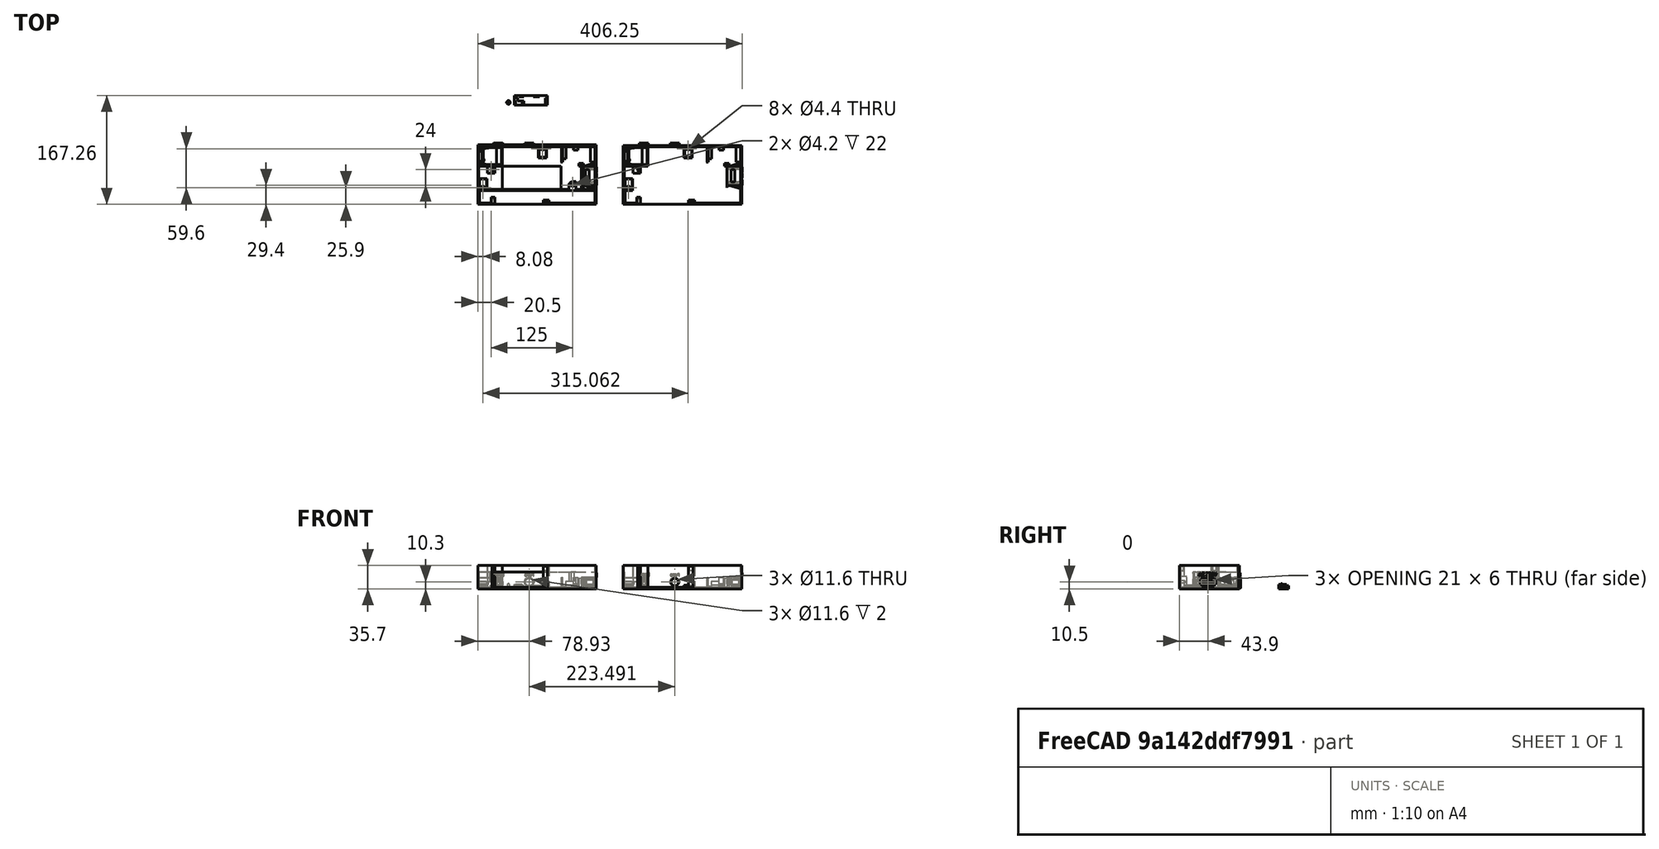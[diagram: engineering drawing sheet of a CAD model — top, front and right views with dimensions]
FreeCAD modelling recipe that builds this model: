
FCSTD DOCUMENT  (FreeCAD 0.19R)
Label: station.pump.1x12V
License: All rights reserved
LicenseURL: http://en.wikipedia.org/wiki/All_rights_reserved
objects: Part::Extrusion×91, Part::Feature×66, Part::MultiFuse×48, Part::Part2DObjectPython×42, Part::Cut×35, Part::FeaturePython×18, Part::Refine×12, Part::Cone×2, App::DocumentObjectGroup×2
note: 314 computed .brp shape members not serialized (recipe doc carries the construction recipe); baked Part::Feature solids carry a one-line shape summary decoded from their .brp

FEATURE [Part::Cut] Cut008
FEATURE [Part::Feature] Cut008_solid  label="Cut008 (Solid)"
  shape: bbox 182.8 x 74.77 x 26 mm, 631 faces (baked)
FEATURE [Part::Feature] Fusion005002002014004003003002009002010004002003006003008008004007002004008002005001  label="Fusion005002002014004003003002009002010004002003006003008008004007002004008002006"
  Placement = pos=(-44.5951,70.6176,187.501) rot=(0,0,1;1.5708rad)
  shape: bbox 50.9 x 14.8 x 7 mm, 30 faces (baked)
FEATURE [Part::MultiFuse] Fusion005002002014004003003002009002010004002003006003008008004007002004008002003
  Placement = pos=(333.004,49.2743,2.13395) rot=(0,0,1;0rad)
FEATURE [Part::Part2DObjectPython] Rectangle  # Draft 2D object (typed FeaturePython)
  Area = 4964
  ChamferSize = 0
  Columns = 1
  FilletRadius = 0
  Height = 136
  Length = 36.5
  MakeFace = true
  Placement = pos=(136,3,22) rot=(0,0,1;1.5708rad)
  Rows = 1
FEATURE [Part::Extrusion] Extrusion
  Base = -> Rectangle
  Dir = (-8.1519e-11,-1.28811e-08,-2)
  DirMode = 0
  FaceMakerClass = Part::FaceMakerBullseye
  LengthFwd = 0
  LengthRev = 0
  Solid = true
  Symmetric = false
FEATURE [Part::Cut] Cut
  Base = -> Cut008_solid
  Tool = -> Extrusion
FEATURE [Part::Part2DObjectPython] Rectangle001  # Draft 2D object (typed FeaturePython)
  Area = 5003.74
  ChamferSize = 0
  Columns = 1
  FilletRadius = 0
  Height = 49.6839
  Length = 100.711
  MakeFace = true
  Placement = pos=(166.761,-20.8491,-24.6542) rot=(0.57735,0.57735,0.57735;2.0944rad)
  Rows = 1
FEATURE [Part::FeaturePython] Slice  # WARN: FeaturePython — macro-defined, semantics opaque (R4)
  Base = -> Cut
  Mode = 1
  Tolerance = 0
  Tools = -> [Rectangle001]
FEATURE [Part::FeaturePython] Slice_child0  label="Slice.0"  # WARN: FeaturePython — macro-defined, semantics opaque (R4)
  Base = -> Slice
  FilterType = 1
  Invert = false
  OverrideMaxVal = 0
  WindowFrom = 80
  WindowTo = 100
  items = 0
FEATURE [Part::FeaturePython] Slice_child1  label="Slice.1"  # WARN: FeaturePython — macro-defined, semantics opaque (R4)
  Base = -> Slice
  FilterType = 1
  Invert = false
  OverrideMaxVal = 0
  WindowFrom = 80
  WindowTo = 100
  items = 1
FEATURE [Part::FeaturePython] Slice_child2  label="Slice.2"  # WARN: FeaturePython — macro-defined, semantics opaque (R4)
  Base = -> Slice
  FilterType = 1
  Invert = false
  OverrideMaxVal = 0
  WindowFrom = 80
  WindowTo = 100
  items = 2
FEATURE [Part::FeaturePython] Slice_child3  label="Slice.3"  # WARN: FeaturePython — macro-defined, semantics opaque (R4)
  Base = -> Slice
  FilterType = 1
  Invert = false
  OverrideMaxVal = 0
  WindowFrom = 80
  WindowTo = 100
  items = 3
FEATURE [Part::FeaturePython] Slice_child4  label="Slice.4"  # WARN: FeaturePython — macro-defined, semantics opaque (R4)
  Base = -> Slice
  FilterType = 1
  Invert = false
  OverrideMaxVal = 0
  WindowFrom = 80
  WindowTo = 100
  items = 4
FEATURE [Part::FeaturePython] Slice_child5  label="Slice.5"  # WARN: FeaturePython — macro-defined, semantics opaque (R4)
  Base = -> Slice
  FilterType = 1
  Invert = false
  OverrideMaxVal = 0
  WindowFrom = 80
  WindowTo = 100
  items = 5
FEATURE [Part::FeaturePython] Slice_child6  label="Slice.6"  # WARN: FeaturePython — macro-defined, semantics opaque (R4)
  Base = -> Slice
  FilterType = 1
  Invert = false
  OverrideMaxVal = 0
  WindowFrom = 80
  WindowTo = 100
  items = 6
FEATURE [Part::MultiFuse] Fusion
  Placement = pos=(4.18709e-10,0,2) rot=(0,0,1;0rad)
  Shapes = -> [Slice_child6,Slice_child5,Slice_child4,Slice_child3,Slice_child2,Slice_child1]
FEATURE [Part::MultiFuse] Fusion005002002014004003003002009002010004002003006003008008004007002004008002005002
  Shapes = -> [Fusion,Slice_child0]
FEATURE [Part::Part2DObjectPython] Wire  # Draft 2D object (typed FeaturePython)
  Area = 5
  ChamferSize = 0
  Closed = true
  End = (131.761,63.6,1.9)
  FilletRadius = 0
  Length = 12.3852
  MakeFace = true
  Placement = pos=(131.761,68.6,1.9) rot=(-0.57735,0.57735,0.57735;4.18879rad)
  Points = (3) [(0,0,0),(5,2,-4.86691e-09),(5,-6.40528e-10,1.95172e-09)]
  Start = (131.761,68.6,1.9)
  Subdivisions = 0
FEATURE [Part::Extrusion] Extrusion001
  Base = -> Wire
  Dir = (7,-8.40441e-09,-2.13773e-08)
  DirMode = 0
  FaceMakerClass = Part::FaceMakerBullseye
  LengthFwd = 0
  LengthRev = 0
  Solid = true
  Symmetric = false
FEATURE [Part::Cut] Cut009
  Base = -> Fusion005002002014004003003002009002010004002003006003008008004007002004008002005002
  Tool = -> Extrusion001
FEATURE [Part::Feature] Face
  shape: bbox 0.0005987 x 24 x 12.2 mm, 1 faces, 0 solids (baked)
FEATURE [Part::Extrusion] Extrusion002
  Base = -> Face
  Dir = (-3,-3e-15,1.56777e-10)
  DirMode = 0
  FaceMakerClass = Part::FaceMakerBullseye
  LengthFwd = 0
  LengthRev = 0
  Solid = true
  Symmetric = false
FEATURE [Part::Cut] Cut010
  Base = -> Cut009
  Tool = -> Extrusion002
FEATURE [Part::Feature] Face001
  shape: bbox 0.0006002 x 33 x 15 mm, 1 faces, 0 solids (baked)
FEATURE [Part::Extrusion] Extrusion004
  Base = -> Face001
  Dir = (-2,1.46e-14,1.04524e-10)
  DirMode = 0
  FaceMakerClass = Part::FaceMakerBullseye
  LengthFwd = 0
  LengthRev = 0
  Solid = true
  Symmetric = false
FEATURE [Part::MultiFuse] Fusion005002002014004003003002009002010004002003006003008008004007002004008002005003
  Shapes = -> [Cut010,Extrusion004]
FEATURE [Part::Feature] Face002
  Placement = pos=(-12.2614,0.5,7.5) rot=(0,0,1;0rad)
  shape: bbox 0.0005987 x 24 x 12.2 mm, 1 faces, 0 solids (baked)
FEATURE [Part::Extrusion] Extrusion005
  Base = -> Face002
  Dir = (1,1e-15,-5.2259e-11)
  DirMode = 0
  FaceMakerClass = Part::FaceMakerBullseye
  LengthFwd = 0
  LengthRev = 0
  Placement = pos=(8.26138,-0.5,-7.5) rot=(0,0,1;0rad)
  Solid = true
  Symmetric = false
FEATURE [Part::Feature] Face003
  Placement = pos=(-2,1.5e-14,1.04524e-10) rot=(0,0,1;0rad)
  shape: bbox 0.0006002 x 33 x 15 mm, 1 faces, 0 solids (baked)
FEATURE [Part::Extrusion] Extrusion006
  Base = -> Face003
  Dir = (-1,7.3e-15,5.22618e-11)
  DirMode = 0
  FaceMakerClass = Part::FaceMakerBullseye
  LengthFwd = 0
  LengthRev = 0
  Solid = true
  Symmetric = false
FEATURE [Part::MultiFuse] Fusion005002002014004003003002009002010004002003006003008008004007002004008002005004
  Shapes = -> [Extrusion006,Extrusion005,Fusion005002002014004003003002009002010004002003006003008008004007002004008002005003]
FEATURE [Part::Cone] Cone
  Angle = 360
  AttacherType = Attacher::AttachEngine3D
  Height = 1.5
  Placement = pos=(-6.92,6,-4) rot=(0,0,1;0rad)
  Radius1 = 3
  Radius2 = 1.5
FEATURE [Part::Cut] Cut011
  Base = -> Fusion005002002014004003003002009002010004002003006003008008004007002004008002005004
  Tool = -> Cone
FEATURE [App::DocumentObjectGroup] GrExplode_Slice  label="Exploded Slice"
  Group = -> [Cut011]
FEATURE [Part::Refine] Cut012
  Source = -> Cut011
FEATURE [Part::Part2DObjectPython] Circle  # Draft 2D object (typed FeaturePython)
  Area = 28.2743
  FirstAngle = 0
  LastAngle = 0
  MakeFace = true
  Placement = pos=(16.73,67.1,4.33988) rot=(1,0,0;1.5708rad)
  Radius = 3
FEATURE [Part::Extrusion] Extrusion007
  Base = -> Circle
  Dir = (3.40484e-11,2,-4.42676e-09)
  DirMode = 0
  FaceMakerClass = Part::FaceMakerBullseye
  LengthFwd = 0
  LengthRev = 0
  Solid = true
  Symmetric = false
FEATURE [Part::Cut] Cut013
  Base = -> Cut012
  Tool = -> Extrusion007
FEATURE [Part::Feature] Face004
  shape: bbox 0.0006002 x 36 x 2.501 mm, 1 faces, 0 solids (baked)
FEATURE [Part::Extrusion] Extrusion008
  Base = -> Face004
  Dir = (-90,-4.77e-14,-2.88e-14)
  DirMode = 0
  FaceMakerClass = Part::FaceMakerBullseye
  LengthFwd = 0
  LengthRev = 0
  Solid = true
  Symmetric = false
FEATURE [Part::MultiFuse] Fusion005002002014004003003002009002010004002003006003008008004007002004008002005005
  Shapes = -> [Extrusion008,Cut013]
FEATURE [Part::Feature] Face005
  shape: bbox 178 x 0.0006002 x 23.5 mm, 1 faces, 0 solids (baked)
FEATURE [Part::Extrusion] Extrusion009
  Base = -> Face005
  Dir = (-1.58296e-10,-30.4599,-8.10578e-10)
  DirMode = 0
  FaceMakerClass = Part::FaceMakerBullseye
  LengthFwd = 0
  LengthRev = 0
  Solid = true
  Symmetric = false
FEATURE [Part::Cut] Cut014
  Base = -> Fusion005002002014004003003002009002010004002003006003008008004007002004008002005005
  Tool = -> Extrusion009
FEATURE [Part::Part2DObjectPython] Rectangle002  # Draft 2D object (typed FeaturePython)
  Area = 1572.37
  ChamferSize = 0
  Columns = 1
  FilletRadius = 0
  Height = 78.7883
  Length = 19.9569
  MakeFace = true
  Placement = pos=(136,1,20) rot=(0,0,1;1.5708rad)
  Rows = 1
FEATURE [Part::Extrusion] Extrusion010
  Base = -> Rectangle002
  Dir = (-8.76339e-10,-1.38472e-07,-21.5)
  DirMode = 0
  FaceMakerClass = Part::FaceMakerBullseye
  LengthFwd = 0
  LengthRev = 0
  Solid = true
  Symmetric = false
FEATURE [Part::Cut] Cut015
  Base = -> Cut014
  Tool = -> Extrusion010
FEATURE [Part::Part2DObjectPython] Rectangle003  # Draft 2D object (typed FeaturePython)
  Area = 5628.58
  ChamferSize = 0
  Columns = 1
  FilletRadius = 0
  Height = 74.0527
  Length = 76.0079
  MakeFace = true
  Placement = pos=(-1.92305e-08,-34.5527,20) rot=(0,0,1;0rad)
  Rows = 1
FEATURE [Part::Extrusion] Extrusion011
  Base = -> Rectangle003
  Dir = (6.9e-15,0,-21.5)
  DirMode = 0
  FaceMakerClass = Part::FaceMakerBullseye
  LengthFwd = 0
  LengthRev = 0
  Solid = true
  Symmetric = false
FEATURE [Part::Cut] Cut016
  Base = -> Cut015
  Tool = -> Extrusion011
FEATURE [Part::Feature] Face006
  shape: bbox 0.0006003 x 2.001 x 20.5 mm, 1 faces, 0 solids (baked)
FEATURE [Part::Extrusion] Extrusion012
  Base = -> Face006
  Dir = (20.0833,-1.0437e-10,0)
  DirMode = 0
  FaceMakerClass = Part::FaceMakerBullseye
  LengthFwd = 0
  LengthRev = 0
  Solid = true
  Symmetric = false
FEATURE [Part::Feature] Face007
  shape: bbox 0.0006003 x 2.001 x 2.001 mm, 1 faces, 0 solids (baked)
FEATURE [Part::Extrusion] Extrusion013
  Base = -> Face007
  Dir = (19.0833,-9.91732e-11,3.32094e-08)
  DirMode = 0
  FaceMakerClass = Part::FaceMakerBullseye
  LengthFwd = 0
  LengthRev = 0
  Solid = true
  Symmetric = false
FEATURE [Part::Feature] Face008
  shape: bbox 0.0006003 x 2.001 x 1.001 mm, 1 faces, 0 solids (baked)
FEATURE [Part::Extrusion] Extrusion014
  Base = -> Face008
  Dir = (20.0833,-1.0437e-10,0)
  DirMode = 0
  FaceMakerClass = Part::FaceMakerBullseye
  LengthFwd = 0
  LengthRev = 0
  Solid = true
  Symmetric = false
FEATURE [Part::MultiFuse] Fusion005002002014004003003002009002010004002003006003008008004007002004008002005006
  Shapes = -> [Extrusion014,Extrusion013,Extrusion012]
FEATURE [Part::Part2DObjectPython] Rectangle004  # Draft 2D object (typed FeaturePython)
  Area = 10
  ChamferSize = 0
  Columns = 1
  FilletRadius = 0
  Height = 5
  Length = 2
  MakeFace = true
  Placement = pos=(11.8133,2.1,-1.5) rot=(0,0,1;1.5708rad)
  Rows = 1
FEATURE [Part::Refine] Cut017
  Source = -> Cut016
FEATURE [Part::Feature] Face009
  shape: bbox 36.27 x 0.0006005 x 23.5 mm, 1 faces, 0 solids (baked)
FEATURE [Part::Extrusion] Extrusion016
  Base = -> Face009
  Dir = (4.92472e-10,-0.5,4.42172e-10)
  DirMode = 0
  FaceMakerClass = Part::FaceMakerBullseye
  LengthFwd = 0
  LengthRev = 0
  Solid = true
  Symmetric = false
FEATURE [Part::MultiFuse] Fusion005002002014004003003002009002010004002003006003008008004007002004008002005007
  Shapes = -> [Cut017,Extrusion016]
FEATURE [Part::Feature] Face010
  shape: bbox 20.08 x 2.001 x 0.0006003 mm, 1 faces, 0 solids (baked)
FEATURE [Part::Extrusion] Extrusion017
  Base = -> Face010
  Dir = (0,-2.5813e-10,9.7)
  DirMode = 0
  FaceMakerClass = Part::FaceMakerBullseye
  LengthFwd = 0
  LengthRev = 0
  Solid = true
  Symmetric = false
FEATURE [Part::MultiFuse] Fusion005002002014004003003002009002010004002003006003008008004007002004008002005008
  Placement = pos=(-5.197e-12,-20.9,2.73057e-07) rot=(0,0,1;0rad)
  Shapes = -> [Fusion005002002014004003003002009002010004002003006003008008004007002004008002005006,Extrusion017]
FEATURE [Part::Feature] Face011
  shape: bbox 181.8 x 0.0006013 x 26 mm, 1 faces, 0 solids (baked)
FEATURE [Part::Extrusion] Extrusion018
  Base = -> Face011
  Dir = (2.8e-15,-19.9,2.2e-15)
  DirMode = 0
  FaceMakerClass = Part::FaceMakerBullseye
  LengthFwd = 0
  LengthRev = 0
  Solid = true
  Symmetric = false
FEATURE [Part::Feature] Face012
  shape: bbox 23 x 1.501 x 0.0006006 mm, 1 faces, 0 solids (baked)
FEATURE [Part::Extrusion] Extrusion019
  Base = -> Face012
  Dir = (3.95367e-10,6.24734e-08,9.7)
  DirMode = 0
  FaceMakerClass = Part::FaceMakerBullseye
  LengthFwd = 0
  LengthRev = 0
  Solid = true
  Symmetric = false
FEATURE [Part::Feature] Face013
  shape: bbox 23 x 0.5006 x 0.0006005 mm, 1 faces, 0 solids (baked)
FEATURE [Part::Extrusion] Extrusion020
  Base = -> Face013
  Dir = (3.95372e-10,8.57813e-09,9.7)
  DirMode = 0
  FaceMakerClass = Part::FaceMakerBullseye
  LengthFwd = 0
  LengthRev = 0
  Solid = true
  Symmetric = false
FEATURE [Part::Part2DObjectPython] Rectangle005  # Draft 2D object (typed FeaturePython)
  Area = 49.5
  ChamferSize = 0
  Columns = 1
  FilletRadius = 0
  Height = 4.5
  Length = 11
  MakeFace = true
  Placement = pos=(11.3133,28,31.7) rot=(0,0,1;1.5708rad)
  Rows = 1
FEATURE [Part::Extrusion] Extrusion021
  Base = -> Rectangle005
  Dir = (-1.35322e-09,-2.13826e-07,-33.2)
  DirMode = 0
  FaceMakerClass = Part::FaceMakerBullseye
  LengthFwd = 0
  LengthRev = 0
  Solid = true
  Symmetric = false
FEATURE [Part::Feature] Face015
  Placement = pos=(11.3133,28,31.7) rot=(0,0,1;1.5708rad)
  shape: bbox 4.5 x 11 x 2.71e-07 mm, 1 faces, 0 solids (baked)
FEATURE [Part::Extrusion] Extrusion022
  Base = -> Face015
  Dir = (-4.07595e-11,-6.44056e-09,-1)
  DirMode = 0
  FaceMakerClass = Part::FaceMakerBullseye
  LengthFwd = 0
  LengthRev = 0
  Solid = true
  Symmetric = false
FEATURE [Part::Cut] Cut018
  Base = -> Extrusion021
  Tool = -> Extrusion022
FEATURE [Part::Refine] Extrusion023
  Source = -> Extrusion018
FEATURE [Part::Feature] Face017
  Placement = pos=(3e-15,-19.9,2e-15) rot=(0,0,1;0rad)
  shape: bbox 181.8 x 0.0006013 x 26 mm, 1 faces, 0 solids (baked)
FEATURE [Part::Extrusion] Extrusion025
  Base = -> Face017
  Dir = (1e-16,-1,1e-16)
  DirMode = 0
  FaceMakerClass = Part::FaceMakerBullseye
  LengthFwd = 0
  LengthRev = 0
  Solid = true
  Symmetric = false
FEATURE [Part::MultiFuse] Fusion005002002014004003003002009002010004002003006003008008004007002004008002005010
  Shapes = -> [Extrusion025,Extrusion023]
FEATURE [Part::Feature] Face018
  shape: bbox 2.001 x 19.9 x 0.0008489 mm, 1 faces, 0 solids (baked)
FEATURE [Part::Extrusion] Extrusion026
  Base = -> Face018
  Dir = (9.73293e-10,1.1e-15,9.7)
  DirMode = 0
  FaceMakerClass = Part::FaceMakerBullseye
  LengthFwd = 0
  LengthRev = 0
  Solid = true
  Symmetric = false
FEATURE [Part::Feature] Face019
  shape: bbox 2.001 x 1.001 x 0.0008489 mm, 1 faces, 0 solids (baked)
FEATURE [Part::Extrusion] Extrusion027
  Base = -> Face019
  Dir = (9.73293e-10,1.1e-15,9.7)
  DirMode = 0
  FaceMakerClass = Part::FaceMakerBullseye
  LengthFwd = 0
  LengthRev = 0
  Solid = true
  Symmetric = false
FEATURE [Part::MultiFuse] Fusion005002002014004003003002009002010004002003006003008008004007002004008002005011
  Shapes = -> [Extrusion026,Extrusion027]
FEATURE [Part::Part2DObjectPython] Rectangle006  # Draft 2D object (typed FeaturePython)
  Area = 145.896
  ChamferSize = 0
  Columns = 1
  FilletRadius = 0
  Height = 2
  Length = 72.9481
  MakeFace = true
  Placement = pos=(164.761,-17.9,31.7) rot=(0,0,1;3.14159rad)
  Rows = 1
FEATURE [Part::Extrusion] Extrusion028
  Base = -> Rectangle006
  Dir = (0,8.83505e-10,-33.2)
  DirMode = 0
  FaceMakerClass = Part::FaceMakerBullseye
  LengthFwd = 0
  LengthRev = 0
  Solid = true
  Symmetric = false
FEATURE [Part::Feature] Face020
  Placement = pos=(85.3133,-18.8,30.7) rot=(0,0,1;0rad)
  shape: bbox 6.5 x 5.5 x 2.001e-07 mm, 1 faces, 0 solids (baked)
FEATURE [Part::Extrusion] Extrusion031
  Base = -> Face020
  Dir = (0,8.56836e-10,-32.2)
  DirMode = 0
  FaceMakerClass = Part::FaceMakerBullseye
  LengthFwd = 0
  LengthRev = 0
  Solid = true
  Symmetric = false
FEATURE [Part::Part2DObjectPython] Rectangle009  # Draft 2D object (typed FeaturePython)
  Area = 76.5
  ChamferSize = 0
  Columns = 1
  FilletRadius = 0
  Height = 17
  Length = 4.5
  MakeFace = true
  Placement = pos=(6.81326,-18.8,-1.5) rot=(1,0,0;1.5708rad)
  Rows = 1
FEATURE [Part::Extrusion] Extrusion032
  Base = -> Rectangle009
  Dir = (0,10,-6.44056e-08)
  DirMode = 0
  FaceMakerClass = Part::FaceMakerBullseye
  LengthFwd = 0
  LengthRev = 0
  Solid = true
  Symmetric = false
FEATURE [Part::MultiFuse] Fusion005002002014004003003002009002010004002003006003008008004007002004008002005012
  Shapes = -> [Fusion005002002014004003003002009002010004002003006003008008004007002004008002005010,Fusion005002002014004003003002009002010004002003006003008008004007002004008002005011]
FEATURE [Part::Feature] Face024
  shape: bbox 12.7 x 2.001 x 0.0006006 mm, 1 faces, 0 solids (baked)
FEATURE [Part::Extrusion] Extrusion033
  Base = -> Face024
  Dir = (-6.05833e-11,-7.98344e-11,3)
  DirMode = 0
  FaceMakerClass = Part::FaceMakerBullseye
  LengthFwd = 0
  LengthRev = 0
  Solid = true
  Symmetric = false
FEATURE [Part::Part2DObjectPython] Rectangle010  # Draft 2D object (typed FeaturePython)
  Area = 214.63
  ChamferSize = 0
  Columns = 1
  FilletRadius = 0
  Height = 16.9
  Length = 12.7
  MakeFace = true
  Placement = pos=(-13.27,3,-1.5) rot=(0,0,1;0rad)
  Rows = 1
FEATURE [Part::Extrusion] Extrusion034
  Base = -> Rectangle010
  Dir = (1.06569e-08,5.14823e-10,1)
  DirMode = 0
  FaceMakerClass = Part::FaceMakerBullseye
  LengthFwd = 0
  LengthRev = 0
  Solid = true
  Symmetric = false
FEATURE [Part::Part2DObjectPython] Circle001  # Draft 2D object (typed FeaturePython)
  Area = 15.2053
  FirstAngle = 0
  LastAngle = 0
  MakeFace = true
  Placement = pos=(-6.92,6,-1.5) rot=(0,0,1;0rad)
  Radius = 2.2
FEATURE [Part::Extrusion] Extrusion035
  Base = -> Circle001
  Dir = (3.19706e-08,1.54447e-09,3)
  DirMode = 0
  FaceMakerClass = Part::FaceMakerBullseye
  LengthFwd = 0
  LengthRev = 0
  Solid = true
  Symmetric = false
FEATURE [Part::Cut] Cut019
  Base = -> Extrusion034
  Tool = -> Extrusion035
FEATURE [Part::MultiFuse] Fusion005002002014004003003002009002010004002003006003008008004007002004008002005013
  Shapes = -> [Cut019,Fusion005002002014004003003002009002010004002003006003008008004007002004008002005007]
FEATURE [Part::MultiFuse] Fusion005002002014004003003002009002010004002003006003008008004007002004008002005014
  Shapes = -> [Fusion005002002014004003003002009002010004002003006003008008004007002004008002005013,Extrusion033]
FEATURE [Part::Feature] Face025
  shape: bbox 2e-07 x 5.5 x 32.2 mm, 1 faces, 0 solids (baked)
FEATURE [Part::Extrusion] Extrusion036
  Base = -> Face025
  Dir = (3,-1.55822e-11,0)
  DirMode = 0
  FaceMakerClass = Part::FaceMakerBullseye
  LengthFwd = 0
  LengthRev = 0
  Solid = true
  Symmetric = false
FEATURE [Part::MultiFuse] Fusion005002002014004003003002009002010004002003006003008008004007002004008002005015
  Shapes = -> [Extrusion031,Extrusion036]
FEATURE [Part::Feature] Face026
  shape: bbox 2.013e-07 x 11 x 32.2 mm, 1 faces, 0 solids (baked)
FEATURE [Part::Extrusion] Extrusion037
  Base = -> Face026
  Dir = (-6.81326,1.5e-15,2.77705e-10)
  DirMode = 0
  FaceMakerClass = Part::FaceMakerBullseye
  LengthFwd = 0
  LengthRev = 0
  Solid = true
  Symmetric = false
FEATURE [Part::Part2DObjectPython] Wire001  # Draft 2D object (typed FeaturePython)
  Area = 63.4773
  ChamferSize = 0
  Closed = true
  End = (11.3133,28,-1.5)
  FilletRadius = 0
  Length = 49.1096
  MakeFace = true
  Placement = pos=(8.31326,28,-1.5) rot=(0.57735,0.57735,0.57735;2.0944rad)
  Points = (4) [(0,0,0),(-1.7945e-07,20,-1.24955e-09),(-1.7945e-07,22.3182,3),(-1.7945e-07,-2.4067e-07,3)]
  Start = (8.31326,28,-1.5)
  Subdivisions = 0
FEATURE [Part::Extrusion] Extrusion038
  Base = -> Wire001
  Dir = (3.07294e-07,11,-2.91789e-08)
  DirMode = 0
  FaceMakerClass = Part::FaceMakerBullseye
  LengthFwd = 0
  LengthRev = 0
  Solid = true
  Symmetric = false
FEATURE [Part::Cut] Cut020
  Base = -> Cut018
  Tool = -> Extrusion038
FEATURE [Part::MultiFuse] Fusion005002002014004003003002009002010004002003006003008008004007002004008002005016
  Shapes = -> [Cut020,Extrusion037]
FEATURE [Part::Part2DObjectPython] Line  # Draft 2D object (typed FeaturePython)
  Area = 0
  ChamferSize = 0
  Closed = false
  End = (10.0133,-18.8,15.5)
  FilletRadius = 0
  Length = 3.2
  MakeFace = true
  Placement = pos=(6.81326,-18.8,15.5) rot=(0,0,1;0rad)
  Points = (2) [(0,0,0),(3.2,0,-7.10543e-15)]
  Start = (6.81326,-18.8,15.5)
  Subdivisions = 0
FEATURE [Part::Part2DObjectPython] Circle002  # Draft 2D object (typed FeaturePython)
  Area = 13.8544
  FirstAngle = 0
  LastAngle = 0
  MakeFace = true
  Placement = pos=(8.91326,-18.8,6.5) rot=(1,0,0;1.5708rad)
  Radius = 2.1
FEATURE [Part::Part2DObjectPython] Line003  # Draft 2D object (typed FeaturePython)
  Area = 0
  ChamferSize = 0
  Closed = false
  End = (6.81326,33.5,30.7)
  FilletRadius = 0
  Length = 5.5
  MakeFace = true
  Placement = pos=(6.81326,39,30.7) rot=(0,0,1;1.5708rad)
  Points = (2) [(0,0,0),(-5.5,-3.55271e-15,0)]
  Start = (6.81326,39,30.7)
  Subdivisions = 0
FEATURE [Part::Part2DObjectPython] Line005  # Draft 2D object (typed FeaturePython)
  Area = 0
  ChamferSize = 0
  Closed = false
  End = (9.81326,33.5,30.7)
  FilletRadius = 0
  Length = 3
  MakeFace = true
  Placement = pos=(6.81326,33.5,30.7) rot=(0,0,1;1.5708rad)
  Points = (2) [(0,0,0),(0,-3,0)]
  Start = (6.81326,33.5,30.7)
  Subdivisions = 0
FEATURE [Part::Part2DObjectPython] Circle003  # Draft 2D object (typed FeaturePython)
  Area = 13.8544
  FirstAngle = 0
  LastAngle = 0
  MakeFace = true
  Placement = pos=(8.91326,33.5,30.7) rot=(0,0,1;1.5708rad)
  Radius = 2.1
FEATURE [Part::MultiFuse] Fusion005002002014004003003002009002010004002003006003008008004007002004008002005017
  Shapes = -> [Fusion005002002014004003003002009002010004002003006003008008004007002004008002005012,Fusion005002002014004003003002009002010004002003006003008008004007002004008002005014]
FEATURE [Part::MultiFuse] Fusion005002002014004003003002009002010004002003006003008008004007002004008002005018
  Shapes = -> [Fusion005002002014004003003002009002010004002003006003008008004007002004008002005017,Extrusion028,Fusion005002002014004003003002009002010004002003006003008008004007002004008002005008,Extrusion032]
FEATURE [Part::MultiFuse] Fusion005002002014004003003002009002010004002003006003008008004007002004008002005019
  Shapes = -> [Fusion005002002014004003003002009002010004002003006003008008004007002004008002005018,Fusion005002002014004003003002009002010004002003006003008008004007002004008002005015,Fusion005002002014004003003002009002010004002003006003008008004007002004008002005016,Extrusion020]
FEATURE [Part::MultiFuse] Fusion005002002014004003003002009002010004002003006003008008004007002004008002005020
  Shapes = -> [Fusion005002002014004003003002009002010004002003006003008008004007002004008002005019,Extrusion019]
FEATURE [Part::Part2DObjectPython] Line007  # Draft 2D object (typed FeaturePython)
  Area = 0
  ChamferSize = 0
  Closed = false
  End = (88.8133,-17.9,-22.1838)
  FilletRadius = 0
  Length = 53.8838
  MakeFace = true
  Placement = pos=(88.8133,-17.9,31.7) rot=(1,0,0;1.5708rad)
  Points = (2) [(0,0,0),(0,-53.8838,-1.06581e-14)]
  Start = (88.8133,-17.9,31.7)
  Subdivisions = 0
FEATURE [Part::Part2DObjectPython] Line008  # Draft 2D object (typed FeaturePython)
  Area = 0
  ChamferSize = 0
  Closed = false
  End = (88.8133,-17.9,30.7)
  FilletRadius = 0
  Length = 3.61386
  MakeFace = true
  Placement = pos=(85.3133,-18.8,30.7) rot=(0,0,1;0rad)
  Points = (2) [(0,0,0),(3.5,0.9,0)]
  Start = (85.3133,-18.8,30.7)
  Subdivisions = 0
FEATURE [Part::Part2DObjectPython] Line009  # Draft 2D object (typed FeaturePython)
  Area = 0
  ChamferSize = 0
  Closed = false
  End = (88.8133,-18.8,30.7)
  FilletRadius = 0
  Length = 0.9
  MakeFace = true
  Placement = pos=(88.8133,-17.9,30.7) rot=(0,0,1;0rad)
  Points = (2) [(0,0,0),(-4.67537e-12,-0.9,0)]
  Start = (88.8133,-17.9,30.7)
  Subdivisions = 0
FEATURE [Part::Part2DObjectPython] Line010  # Draft 2D object (typed FeaturePython)
  Area = 0
  ChamferSize = 0
  Closed = false
  End = (88.8133,-14.8,30.7)
  FilletRadius = 0
  Length = 4
  MakeFace = true
  Placement = pos=(88.8133,-18.8,30.7) rot=(0,0,1;0rad)
  Points = (2) [(0,0,0),(0,4,0)]
  Start = (88.8133,-18.8,30.7)
  Subdivisions = 0
FEATURE [Part::Feature] Face027
  shape: bbox 30.76 x 71.1 x 0.0006012 mm, 1 faces, 0 solids (baked)
FEATURE [Part::Extrusion] Extrusion039
  Base = -> Face027
  Dir = (9.73293e-10,4.2588e-11,9.7)
  DirMode = 0
  FaceMakerClass = Part::FaceMakerBullseye
  LengthFwd = 0
  LengthRev = 0
  Solid = true
  Symmetric = false
FEATURE [Part::Feature] Face028
  shape: bbox 113 x 3.501 x 0.0006009 mm, 1 faces, 0 solids (baked)
FEATURE [Part::Extrusion] Extrusion040
  Base = -> Face028
  Dir = (-3.17982e-08,1.30762e-08,9.7)
  DirMode = 0
  FaceMakerClass = Part::FaceMakerBullseye
  LengthFwd = 0
  LengthRev = 0
  Solid = true
  Symmetric = false
FEATURE [Part::Feature] Face029
  shape: bbox 38 x 71.1 x 0.0006006 mm, 1 faces, 0 solids (baked)
FEATURE [Part::Extrusion] Extrusion041
  Base = -> Face029
  Dir = (-1.47194e-08,4.19602e-08,9.7)
  DirMode = 0
  FaceMakerClass = Part::FaceMakerBullseye
  LengthFwd = 0
  LengthRev = 0
  Solid = true
  Symmetric = false
FEATURE [Part::Feature] Face030
  shape: bbox 1.731 x 19.9 x 0.0006008 mm, 1 faces, 0 solids (baked)
FEATURE [Part::Extrusion] Extrusion042
  Base = -> Face030
  Dir = (4.39548e-09,1.1e-15,9.7)
  DirMode = 0
  FaceMakerClass = Part::FaceMakerBullseye
  LengthFwd = 0
  LengthRev = 0
  Solid = true
  Symmetric = false
FEATURE [Part::MultiFuse] Fusion005002002014004003003002009002010004002003006003008008004007002004008002005021
  Shapes = -> [Extrusion042,Extrusion041,Extrusion040,Extrusion039]
FEATURE [Part::Refine] Fusion005002002014004003003002009002010004002003006003008008004007002004008002005021001
  Source = -> Fusion005002002014004003003002009002010004002003006003008008004007002004008002005021
FEATURE [Part::MultiFuse] Fusion005002002014004003003002009002010004002003006003008008004007002004008002005021002
  Shapes = -> [Fusion005002002014004003003002009002010004002003006003008008004007002004008002005020,Fusion005002002014004003003002009002010004002003006003008008004007002004008002005021001]
FEATURE [Part::Refine] Fusion005002002014004003003002009002010004002003006003008008004007002004008002005021002001
  Source = -> Fusion005002002014004003003002009002010004002003006003008008004007002004008002005021002
FEATURE [Part::Feature] Face031
  shape: bbox 0.000602 x 9.101 x 17 mm, 1 faces, 0 solids (baked)
FEATURE [Part::Extrusion] Extrusion043
  Base = -> Face031
  Dir = (-1,0,4.07599e-11)
  DirMode = 0
  FaceMakerClass = Part::FaceMakerBullseye
  LengthFwd = 0
  LengthRev = 0
  Solid = true
  Symmetric = false
FEATURE [Part::MultiFuse] Fusion005002002014004003003002009002010004002003006003008008004007002004008002005021002002
  Shapes = -> [Fusion005002002014004003003002009002010004002003006003008008004007002004008002005021002001,Extrusion043]
FEATURE [Part::Extrusion] Extrusion044
  Base = -> Circle002
  Dir = (6e-16,7,-4.50839e-08)
  DirMode = 0
  FaceMakerClass = Part::FaceMakerBullseye
  LengthFwd = 0
  LengthRev = 0
  Solid = true
  Symmetric = false
FEATURE [Part::Cut] Cut021
  Base = -> Fusion005002002014004003003002009002010004002003006003008008004007002004008002005021002002
  Tool = -> Extrusion044
FEATURE [Part::Part2DObjectPython] Line006  # Draft 2D object (typed FeaturePython)
  Area = 0
  ChamferSize = 0
  Closed = false
  End = (88.8133,-17.9,31.7)
  FilletRadius = 0
  Length = 82
  MakeFace = true
  Placement = pos=(6.81326,-17.9,31.7) rot=(0,0,1;1.5708rad)
  Points = (2) [(0,0,0),(3.19744e-14,-82,-7.10543e-15)]
  Start = (6.81326,-17.9,31.7)
  Subdivisions = 0
FEATURE [Part::Feature] Face032
  shape: bbox 1.731 x 1.001 x 0.0008489 mm, 1 faces, 0 solids (baked)
FEATURE [Part::Extrusion] Extrusion045
  Base = -> Face032
  Dir = (4.39548e-09,1.1e-15,9.7)
  DirMode = 0
  FaceMakerClass = Part::FaceMakerBullseye
  LengthFwd = 0
  LengthRev = 0
  Solid = true
  Symmetric = false
FEATURE [Part::MultiFuse] Fusion005002002014004003003002009002010004002003006003008008004007002004008002005021002003
  Shapes = -> [Extrusion045,Cut021]
FEATURE [Part::Part2DObjectPython] Circle004  # Draft 2D object (typed FeaturePython)
  Area = 13.8544
  FirstAngle = 0
  LastAngle = 0
  MakeFace = true
  Placement = pos=(88.8133,-15.8,30.7) rot=(0,0,1;0rad)
  Radius = 2.1
FEATURE [Part::Part2DObjectPython] Line011  # Draft 2D object (typed FeaturePython)
  Area = 0
  ChamferSize = 0
  Closed = false
  End = (88.8133,89.5489,30.7)
  FilletRadius = 0
  Length = 104.349
  MakeFace = true
  Placement = pos=(88.8133,-14.8,30.7) rot=(0,0,1;0rad)
  Points = (2) [(0,0,0),(0,104.349,0)]
  Start = (88.8133,-14.8,30.7)
  Subdivisions = 0
FEATURE [Part::Extrusion] Extrusion046
  Base = -> Circle004
  Dir = (0,1.86269e-10,-7)
  DirMode = 0
  FaceMakerClass = Part::FaceMakerBullseye
  LengthFwd = 0
  LengthRev = 0
  Solid = true
  Symmetric = false
FEATURE [Part::Cut] Cut022
  Base = -> Fusion005002002014004003003002009002010004002003006003008008004007002004008002005021002003
  Tool = -> Extrusion046
FEATURE [Part::Extrusion] Extrusion047
  Base = -> Circle003
  Dir = (-2.85319e-10,-4.50839e-08,-7)
  DirMode = 0
  FaceMakerClass = Part::FaceMakerBullseye
  LengthFwd = 0
  LengthRev = 0
  Solid = true
  Symmetric = false
FEATURE [Part::Cut] Cut023
  Base = -> Cut022
  Tool = -> Extrusion047
FEATURE [Part::Refine] Cut023001
  Source = -> Cut023
FEATURE [Part::Part2DObjectPython] Line012  # Draft 2D object (typed FeaturePython)
  Area = 0
  ChamferSize = 0
  Closed = false
  End = (164.761,70.6,31.7)
  FilletRadius = 0
  Length = 2
  MakeFace = true
  Placement = pos=(164.761,68.6,31.7) rot=(0,0,1;0rad)
  Points = (2) [(0,0,0),(0,2,0)]
  Start = (164.761,68.6,31.7)
  Subdivisions = 0
FEATURE [Part::Feature] Face034
  shape: bbox 0.000602 x 9.101 x 17 mm, 1 faces, 0 solids (baked)
FEATURE [Part::Feature] Face035
  shape: bbox 0.0006003 x 2.001 x 1.001 mm, 1 faces, 0 solids (baked)
FEATURE [Part::Feature] Face036
  shape: bbox 0.0006003 x 2.001 x 20.5 mm, 1 faces, 0 solids (baked)
FEATURE [Part::Part2DObjectPython] Rectangle011  # Draft 2D object (typed FeaturePython)
  Area = 1572.37
  ChamferSize = 0
  Columns = 1
  FilletRadius = 0
  Height = 78.7883
  Length = 19.9569
  MakeFace = true
  Placement = pos=(136,1,20) rot=(0,0,1;1.5708rad)
  Rows = 1
FEATURE [Part::Feature] Face037
  shape: bbox 0.0006002 x 33 x 15 mm, 1 faces, 0 solids (baked)
FEATURE [Part::Feature] Face038
  shape: bbox 2.013e-07 x 11 x 32.2 mm, 1 faces, 0 solids (baked)
FEATURE [Part::Part2DObjectPython] Circle005  # Draft 2D object (typed FeaturePython)
  Area = 28.2743
  FirstAngle = 0
  LastAngle = 0
  MakeFace = true
  Placement = pos=(16.73,67.1,4.33988) rot=(1,0,0;1.5708rad)
  Radius = 3
FEATURE [Part::Feature] Face039
  shape: bbox 0.0006003 x 2.001 x 2.001 mm, 1 faces, 0 solids (baked)
FEATURE [Part::Feature] Face040
  shape: bbox 12.7 x 2.001 x 0.0006006 mm, 1 faces, 0 solids (baked)
FEATURE [Part::Feature] Face041
  shape: bbox 36.27 x 0.0006005 x 23.5 mm, 1 faces, 0 solids (baked)
FEATURE [Part::Feature] Face042
  shape: bbox 2e-07 x 5.5 x 32.2 mm, 1 faces, 0 solids (baked)
FEATURE [Part::Feature] Face043
  shape: bbox 2.001 x 1.001 x 0.0008489 mm, 1 faces, 0 solids (baked)
FEATURE [Part::Feature] Face044
  Placement = pos=(11.3133,28,31.7) rot=(0,0,1;1.5708rad)
  shape: bbox 4.5 x 11 x 2.71e-07 mm, 1 faces, 0 solids (baked)
FEATURE [Part::Extrusion] Extrusion055
  Base = -> Face044
  Dir = (-4.07595e-11,-6.44056e-09,-1)
  DirMode = 0
  FaceMakerClass = Part::FaceMakerBullseye
  LengthFwd = 0
  LengthRev = 0
  Solid = true
  Symmetric = false
FEATURE [Part::Feature] Face045
  shape: bbox 30.76 x 71.1 x 0.0006012 mm, 1 faces, 0 solids (baked)
FEATURE [Part::Feature] Face046
  shape: bbox 20.08 x 2.001 x 0.0006003 mm, 1 faces, 0 solids (baked)
FEATURE [Part::Part2DObjectPython] Rectangle012  # Draft 2D object (typed FeaturePython)
  Area = 145.896
  ChamferSize = 0
  Columns = 1
  FilletRadius = 0
  Height = 2
  Length = 72.9481
  MakeFace = true
  Placement = pos=(164.761,-17.9,31.7) rot=(0,0,1;3.14159rad)
  Rows = 1
FEATURE [Part::Extrusion] Extrusion054
  Base = -> Rectangle012
  Dir = (0,8.83505e-10,-33.2)
  DirMode = 0
  FaceMakerClass = Part::FaceMakerBullseye
  LengthFwd = 0
  LengthRev = 0
  Solid = true
  Symmetric = false
FEATURE [Part::Part2DObjectPython] Rectangle013  # Draft 2D object (typed FeaturePython)
  Area = 5628.58
  ChamferSize = 0
  Columns = 1
  FilletRadius = 0
  Height = 74.0527
  Length = 76.0079
  MakeFace = true
  Placement = pos=(-1.92305e-08,-34.5527,20) rot=(0,0,1;0rad)
  Rows = 1
FEATURE [Part::Part2DObjectPython] Rectangle014  # Draft 2D object (typed FeaturePython)
  Area = 4964
  ChamferSize = 0
  Columns = 1
  FilletRadius = 0
  Height = 136
  Length = 36.5
  MakeFace = true
  Placement = pos=(136,3,22) rot=(0,0,1;1.5708rad)
  Rows = 1
FEATURE [Part::Feature] Face047
  Placement = pos=(85.3133,-18.8,30.7) rot=(0,0,1;0rad)
  shape: bbox 6.5 x 5.5 x 2.001e-07 mm, 1 faces, 0 solids (baked)
FEATURE [Part::Extrusion] Extrusion052
  Base = -> Face047
  Dir = (0,8.56836e-10,-32.2)
  DirMode = 0
  FaceMakerClass = Part::FaceMakerBullseye
  LengthFwd = 0
  LengthRev = 0
  Solid = true
  Symmetric = false
FEATURE [Part::Extrusion] Extrusion058
  Base = -> Face040
  Dir = (-6.05833e-11,-7.98344e-11,3)
  DirMode = 0
  FaceMakerClass = Part::FaceMakerBullseye
  LengthFwd = 0
  LengthRev = 0
  Solid = true
  Symmetric = false
FEATURE [Part::Extrusion] Extrusion061
  Base = -> Rectangle013
  Dir = (6.9e-15,0,-21.5)
  DirMode = 0
  FaceMakerClass = Part::FaceMakerBullseye
  LengthFwd = 0
  LengthRev = 0
  Solid = true
  Symmetric = false
FEATURE [Part::Feature] Face048
  Placement = pos=(3e-15,-19.9,2e-15) rot=(0,0,1;0rad)
  shape: bbox 181.8 x 0.0006013 x 26 mm, 1 faces, 0 solids (baked)
FEATURE [Part::Extrusion] Extrusion050
  Base = -> Face048
  Dir = (1e-16,-1,1e-16)
  DirMode = 0
  FaceMakerClass = Part::FaceMakerBullseye
  LengthFwd = 0
  LengthRev = 0
  Solid = true
  Symmetric = false
FEATURE [Part::Extrusion] Extrusion063
  Base = -> Face036
  Dir = (20.0833,-1.0437e-10,0)
  DirMode = 0
  FaceMakerClass = Part::FaceMakerBullseye
  LengthFwd = 0
  LengthRev = 0
  Solid = true
  Symmetric = false
FEATURE [Part::Extrusion] Extrusion064
  Base = -> Face034
  Dir = (-1,0,4.07599e-11)
  DirMode = 0
  FaceMakerClass = Part::FaceMakerBullseye
  LengthFwd = 0
  LengthRev = 0
  Solid = true
  Symmetric = false
FEATURE [Part::Part2DObjectPython] Rectangle015  # Draft 2D object (typed FeaturePython)
  Area = 214.63
  ChamferSize = 0
  Columns = 1
  FilletRadius = 0
  Height = 16.9
  Length = 12.7
  MakeFace = true
  Placement = pos=(-13.27,3,-1.5) rot=(0,0,1;0rad)
  Rows = 1
FEATURE [Part::Feature] Face049
  Placement = pos=(-12.2614,0.5,7.5) rot=(0,0,1;0rad)
  shape: bbox 0.0005987 x 24 x 12.2 mm, 1 faces, 0 solids (baked)
FEATURE [Part::Extrusion] Extrusion059
  Base = -> Face049
  Dir = (1,1e-15,-5.2259e-11)
  DirMode = 0
  FaceMakerClass = Part::FaceMakerBullseye
  LengthFwd = 0
  LengthRev = 0
  Placement = pos=(8.26138,-0.5,-7.5) rot=(0,0,1;0rad)
  Solid = true
  Symmetric = false
FEATURE [Part::Feature] Face050
  shape: bbox 1.731 x 1.001 x 0.0008489 mm, 1 faces, 0 solids (baked)
FEATURE [Part::Extrusion] Extrusion066
  Base = -> Face050
  Dir = (4.39548e-09,1.1e-15,9.7)
  DirMode = 0
  FaceMakerClass = Part::FaceMakerBullseye
  LengthFwd = 0
  LengthRev = 0
  Solid = true
  Symmetric = false
FEATURE [Part::Part2DObjectPython] Rectangle016  # Draft 2D object (typed FeaturePython)
  Area = 5003.74
  ChamferSize = 0
  Columns = 1
  FilletRadius = 0
  Height = 49.6839
  Length = 100.711
  MakeFace = true
  Placement = pos=(166.761,-20.8491,-24.6542) rot=(0.57735,0.57735,0.57735;2.0944rad)
  Rows = 1
FEATURE [Part::Extrusion] Extrusion068
  Base = -> Face045
  Dir = (9.73293e-10,4.2588e-11,9.7)
  DirMode = 0
  FaceMakerClass = Part::FaceMakerBullseye
  LengthFwd = 0
  LengthRev = 0
  Solid = true
  Symmetric = false
FEATURE [Part::Part2DObjectPython] Rectangle017  # Draft 2D object (typed FeaturePython)
  Area = 49.5
  ChamferSize = 0
  Columns = 1
  FilletRadius = 0
  Height = 4.5
  Length = 11
  MakeFace = true
  Placement = pos=(11.3133,28,31.7) rot=(0,0,1;1.5708rad)
  Rows = 1
FEATURE [Part::Feature] Face051
  Placement = pos=(-2,1.5e-14,1.04524e-10) rot=(0,0,1;0rad)
  shape: bbox 0.0006002 x 33 x 15 mm, 1 faces, 0 solids (baked)
FEATURE [Part::Extrusion] Extrusion065
  Base = -> Face051
  Dir = (-1,7.3e-15,5.22618e-11)
  DirMode = 0
  FaceMakerClass = Part::FaceMakerBullseye
  LengthFwd = 0
  LengthRev = 0
  Solid = true
  Symmetric = false
FEATURE [Part::Extrusion] Extrusion069
  Base = -> Face037
  Dir = (-2,1.46e-14,1.04524e-10)
  DirMode = 0
  FaceMakerClass = Part::FaceMakerBullseye
  LengthFwd = 0
  LengthRev = 0
  Solid = true
  Symmetric = false
FEATURE [Part::Feature] Face052
  shape: bbox 113 x 3.501 x 0.0006009 mm, 1 faces, 0 solids (baked)
FEATURE [Part::Feature] Face053
  shape: bbox 0.0005987 x 24 x 12.2 mm, 1 faces, 0 solids (baked)
FEATURE [Part::Extrusion] Extrusion057
  Base = -> Face053
  Dir = (-3,-3e-15,1.56777e-10)
  DirMode = 0
  FaceMakerClass = Part::FaceMakerBullseye
  LengthFwd = 0
  LengthRev = 0
  Solid = true
  Symmetric = false
FEATURE [Part::Extrusion] Extrusion072
  Base = -> Face039
  Dir = (19.0833,-9.91732e-11,3.32094e-08)
  DirMode = 0
  FaceMakerClass = Part::FaceMakerBullseye
  LengthFwd = 0
  LengthRev = 0
  Solid = true
  Symmetric = false
FEATURE [Part::Feature] Face054
  shape: bbox 0.0006002 x 36 x 2.501 mm, 1 faces, 0 solids (baked)
FEATURE [Part::Extrusion] Extrusion071
  Base = -> Face054
  Dir = (-90,-4.77e-14,-2.88e-14)
  DirMode = 0
  FaceMakerClass = Part::FaceMakerBullseye
  LengthFwd = 0
  LengthRev = 0
  Solid = true
  Symmetric = false
FEATURE [Part::Extrusion] Extrusion073
  Base = -> Face046
  Dir = (0,-2.5813e-10,9.7)
  DirMode = 0
  FaceMakerClass = Part::FaceMakerBullseye
  LengthFwd = 0
  LengthRev = 0
  Solid = true
  Symmetric = false
FEATURE [Part::Feature] Face055
  shape: bbox 23 x 0.5006 x 0.0006005 mm, 1 faces, 0 solids (baked)
FEATURE [Part::Extrusion] Extrusion053
  Base = -> Face055
  Dir = (3.95372e-10,8.57813e-09,9.7)
  DirMode = 0
  FaceMakerClass = Part::FaceMakerBullseye
  LengthFwd = 0
  LengthRev = 0
  Solid = true
  Symmetric = false
FEATURE [Part::Part2DObjectPython] Circle006  # Draft 2D object (typed FeaturePython)
  Area = 13.8544
  FirstAngle = 0
  LastAngle = 0
  MakeFace = true
  Placement = pos=(88.8133,-15.8,30.7) rot=(0,0,1;0rad)
  Radius = 2.1
FEATURE [Part::Feature] Face056
  shape: bbox 181.8 x 0.0006013 x 26 mm, 1 faces, 0 solids (baked)
FEATURE [Part::Extrusion] Extrusion076
  Base = -> Face042
  Dir = (3,-1.55822e-11,0)
  DirMode = 0
  FaceMakerClass = Part::FaceMakerBullseye
  LengthFwd = 0
  LengthRev = 0
  Solid = true
  Symmetric = false
FEATURE [Part::MultiFuse] Fusion005002002014004003003002009002010004002003006003008008004007002004008002005021002012
  Shapes = -> [Extrusion052,Extrusion076]
FEATURE [Part::Extrusion] Extrusion077
  Base = -> Face043
  Dir = (9.73293e-10,1.1e-15,9.7)
  DirMode = 0
  FaceMakerClass = Part::FaceMakerBullseye
  LengthFwd = 0
  LengthRev = 0
  Solid = true
  Symmetric = false
FEATURE [Part::Feature] Cut008_solid001  label="Cut008 (Solid)001"
  shape: bbox 182.8 x 74.77 x 26 mm, 631 faces (baked)
FEATURE [Part::Extrusion] Extrusion078
  Base = -> Rectangle011
  Dir = (-8.76339e-10,-1.38472e-07,-21.5)
  DirMode = 0
  FaceMakerClass = Part::FaceMakerBullseye
  LengthFwd = 0
  LengthRev = 0
  Solid = true
  Symmetric = false
FEATURE [Part::Extrusion] Extrusion079
  Base = -> Face035
  Dir = (20.0833,-1.0437e-10,0)
  DirMode = 0
  FaceMakerClass = Part::FaceMakerBullseye
  LengthFwd = 0
  LengthRev = 0
  Solid = true
  Symmetric = false
FEATURE [Part::MultiFuse] Fusion005002002014004003003002009002010004002003006003008008004007002004008002005021002011
  Shapes = -> [Extrusion079,Extrusion072,Extrusion063]
FEATURE [Part::Feature] Face057
  shape: bbox 1.731 x 19.9 x 0.0006008 mm, 1 faces, 0 solids (baked)
FEATURE [Part::Extrusion] Extrusion080
  Base = -> Rectangle015
  Dir = (1.06569e-08,5.14823e-10,1)
  DirMode = 0
  FaceMakerClass = Part::FaceMakerBullseye
  LengthFwd = 0
  LengthRev = 0
  Solid = true
  Symmetric = false
FEATURE [Part::Part2DObjectPython] Rectangle018  # Draft 2D object (typed FeaturePython)
  Area = 76.5
  ChamferSize = 0
  Columns = 1
  FilletRadius = 0
  Height = 17
  Length = 4.5
  MakeFace = true
  Placement = pos=(6.81326,-18.8,-1.5) rot=(1,0,0;1.5708rad)
  Rows = 1
FEATURE [Part::Extrusion] Extrusion060
  Base = -> Rectangle018
  Dir = (0,10,-6.44056e-08)
  DirMode = 0
  FaceMakerClass = Part::FaceMakerBullseye
  LengthFwd = 0
  LengthRev = 0
  Solid = true
  Symmetric = false
FEATURE [Part::Extrusion] Extrusion081
  Base = -> Circle005
  Dir = (3.40484e-11,2,-4.42676e-09)
  DirMode = 0
  FaceMakerClass = Part::FaceMakerBullseye
  LengthFwd = 0
  LengthRev = 0
  Solid = true
  Symmetric = false
FEATURE [Part::Extrusion] Extrusion082
  Base = -> Face041
  Dir = (4.92472e-10,-0.5,4.42172e-10)
  DirMode = 0
  FaceMakerClass = Part::FaceMakerBullseye
  LengthFwd = 0
  LengthRev = 0
  Solid = true
  Symmetric = false
FEATURE [Part::Extrusion] Extrusion083
  Base = -> Rectangle014
  Dir = (-8.1519e-11,-1.28811e-08,-2)
  DirMode = 0
  FaceMakerClass = Part::FaceMakerBullseye
  LengthFwd = 0
  LengthRev = 0
  Solid = true
  Symmetric = false
FEATURE [Part::Cut] Cut023005
  Base = -> Cut008_solid001
  Tool = -> Extrusion083
FEATURE [Part::FeaturePython] Slice001  # WARN: FeaturePython — macro-defined, semantics opaque (R4)
  Base = -> Cut023005
  Mode = 1
  Tolerance = 0
  Tools = -> [Rectangle016]
FEATURE [Part::FeaturePython] Slice_child007  label="Slice.007"  # WARN: FeaturePython — macro-defined, semantics opaque (R4)
  Base = -> Slice001
  FilterType = 1
  Invert = false
  OverrideMaxVal = 0
  WindowFrom = 80
  WindowTo = 100
  items = 1
FEATURE [Part::FeaturePython] Slice_child008  label="Slice.008"  # WARN: FeaturePython — macro-defined, semantics opaque (R4)
  Base = -> Slice001
  FilterType = 1
  Invert = false
  OverrideMaxVal = 0
  WindowFrom = 80
  WindowTo = 100
  items = 2
FEATURE [Part::FeaturePython] Slice_child009  label="Slice.009"  # WARN: FeaturePython — macro-defined, semantics opaque (R4)
  Base = -> Slice001
  FilterType = 1
  Invert = false
  OverrideMaxVal = 0
  WindowFrom = 80
  WindowTo = 100
  items = 5
FEATURE [Part::FeaturePython] Slice_child010  label="Slice.010"  # WARN: FeaturePython — macro-defined, semantics opaque (R4)
  Base = -> Slice001
  FilterType = 1
  Invert = false
  OverrideMaxVal = 0
  WindowFrom = 80
  WindowTo = 100
  items = 0
FEATURE [Part::FeaturePython] Slice_child011  label="Slice.011"  # WARN: FeaturePython — macro-defined, semantics opaque (R4)
  Base = -> Slice001
  FilterType = 1
  Invert = false
  OverrideMaxVal = 0
  WindowFrom = 80
  WindowTo = 100
  items = 3
FEATURE [Part::FeaturePython] Slice_child012  label="Slice.012"  # WARN: FeaturePython — macro-defined, semantics opaque (R4)
  Base = -> Slice001
  FilterType = 1
  Invert = false
  OverrideMaxVal = 0
  WindowFrom = 80
  WindowTo = 100
  items = 6
FEATURE [Part::FeaturePython] Slice_child013  label="Slice.013"  # WARN: FeaturePython — macro-defined, semantics opaque (R4)
  Base = -> Slice001
  FilterType = 1
  Invert = false
  OverrideMaxVal = 0
  WindowFrom = 80
  WindowTo = 100
  items = 4
FEATURE [Part::MultiFuse] Fusion005002002014004003003002009002010004002003006003008008004007002004008002005021002020
  Placement = pos=(4.18709e-10,0,2) rot=(0,0,1;0rad)
  Shapes = -> [Slice_child012,Slice_child009,Slice_child013,Slice_child011,Slice_child008,Slice_child007]
FEATURE [Part::MultiFuse] Fusion005002002014004003003002009002010004002003006003008008004007002004008002005021002019
  Shapes = -> [Fusion005002002014004003003002009002010004002003006003008008004007002004008002005021002020,Slice_child010]
FEATURE [Part::Feature] Face058
  shape: bbox 38 x 71.1 x 0.0006006 mm, 1 faces, 0 solids (baked)
FEATURE [Part::Extrusion] Extrusion074
  Base = -> Face058
  Dir = (-1.47194e-08,4.19602e-08,9.7)
  DirMode = 0
  FaceMakerClass = Part::FaceMakerBullseye
  LengthFwd = 0
  LengthRev = 0
  Solid = true
  Symmetric = false
FEATURE [Part::Extrusion] Extrusion085
  Base = -> Face052
  Dir = (-3.17982e-08,1.30762e-08,9.7)
  DirMode = 0
  FaceMakerClass = Part::FaceMakerBullseye
  LengthFwd = 0
  LengthRev = 0
  Solid = true
  Symmetric = false
FEATURE [Part::Feature] Face059
  shape: bbox 23 x 1.501 x 0.0006006 mm, 1 faces, 0 solids (baked)
FEATURE [Part::Extrusion] Extrusion067
  Base = -> Face059
  Dir = (3.95367e-10,6.24734e-08,9.7)
  DirMode = 0
  FaceMakerClass = Part::FaceMakerBullseye
  LengthFwd = 0
  LengthRev = 0
  Solid = true
  Symmetric = false
FEATURE [Part::Extrusion] Extrusion086
  Base = -> Rectangle017
  Dir = (-1.35322e-09,-2.13826e-07,-33.2)
  DirMode = 0
  FaceMakerClass = Part::FaceMakerBullseye
  LengthFwd = 0
  LengthRev = 0
  Solid = true
  Symmetric = false
FEATURE [Part::Cut] Cut023010
  Base = -> Extrusion086
  Tool = -> Extrusion055
FEATURE [Part::Extrusion] Extrusion087
  Base = -> Face057
  Dir = (4.39548e-09,1.1e-15,9.7)
  DirMode = 0
  FaceMakerClass = Part::FaceMakerBullseye
  LengthFwd = 0
  LengthRev = 0
  Solid = true
  Symmetric = false
FEATURE [Part::MultiFuse] Fusion005002002014004003003002009002010004002003006003008008004007002004008002005021002024
  Shapes = -> [Extrusion087,Extrusion074,Extrusion085,Extrusion068]
FEATURE [Part::Refine] Fusion005002002014004003003002009002010004002003006003008008004007002004008002005021002007
  Source = -> Fusion005002002014004003003002009002010004002003006003008008004007002004008002005021002024
FEATURE [Part::Part2DObjectPython] Circle007  # Draft 2D object (typed FeaturePython)
  Area = 13.8544
  FirstAngle = 0
  LastAngle = 0
  MakeFace = true
  Placement = pos=(8.91326,33.5,30.7) rot=(0,0,1;1.5708rad)
  Radius = 2.1
FEATURE [Part::Cone] Cone001
  Angle = 360
  AttacherType = Attacher::AttachEngine3D
  Height = 1.5
  Placement = pos=(-6.92,6,-4) rot=(0,0,1;0rad)
  Radius1 = 3
  Radius2 = 1.5
FEATURE [Part::Part2DObjectPython] Circle008  # Draft 2D object (typed FeaturePython)
  Area = 13.8544
  FirstAngle = 0
  LastAngle = 0
  MakeFace = true
  Placement = pos=(8.91326,-18.8,6.5) rot=(1,0,0;1.5708rad)
  Radius = 2.1
FEATURE [Part::Extrusion] Extrusion070
  Base = -> Circle008
  Dir = (6e-16,7,-4.50839e-08)
  DirMode = 0
  FaceMakerClass = Part::FaceMakerBullseye
  LengthFwd = 0
  LengthRev = 0
  Solid = true
  Symmetric = false
FEATURE [Part::Part2DObjectPython] Wire002  # Draft 2D object (typed FeaturePython)
  Area = 5
  ChamferSize = 0
  Closed = true
  End = (131.761,63.6,1.9)
  FilletRadius = 0
  Length = 12.3852
  MakeFace = true
  Placement = pos=(131.761,68.6,1.9) rot=(-0.57735,0.57735,0.57735;4.18879rad)
  Points = (3) [(0,0,0),(5,2,-4.86691e-09),(5,-6.40528e-10,1.95172e-09)]
  Start = (131.761,68.6,1.9)
  Subdivisions = 0
FEATURE [Part::Extrusion] Extrusion075
  Base = -> Wire002
  Dir = (7,-8.40441e-09,-2.13773e-08)
  DirMode = 0
  FaceMakerClass = Part::FaceMakerBullseye
  LengthFwd = 0
  LengthRev = 0
  Solid = true
  Symmetric = false
FEATURE [Part::Cut] Cut023004
  Base = -> Fusion005002002014004003003002009002010004002003006003008008004007002004008002005021002019
  Tool = -> Extrusion075
FEATURE [Part::Cut] Cut023017
  Base = -> Cut023004
  Tool = -> Extrusion057
FEATURE [Part::Part2DObjectPython] Circle009  # Draft 2D object (typed FeaturePython)
  Area = 15.2053
  FirstAngle = 0
  LastAngle = 0
  MakeFace = true
  Placement = pos=(-6.92,6,-1.5) rot=(0,0,1;0rad)
  Radius = 2.2
FEATURE [Part::Extrusion] Extrusion051
  Base = -> Circle009
  Dir = (3.19706e-08,1.54447e-09,3)
  DirMode = 0
  FaceMakerClass = Part::FaceMakerBullseye
  LengthFwd = 0
  LengthRev = 0
  Solid = true
  Symmetric = false
FEATURE [Part::Cut] Cut023003
  Base = -> Extrusion080
  Tool = -> Extrusion051
FEATURE [Part::Feature] Face060
  shape: bbox 178 x 0.0006002 x 23.5 mm, 1 faces, 0 solids (baked)
FEATURE [Part::Extrusion] Extrusion062
  Base = -> Face060
  Dir = (-1.58296e-10,-30.4599,-8.10578e-10)
  DirMode = 0
  FaceMakerClass = Part::FaceMakerBullseye
  LengthFwd = 0
  LengthRev = 0
  Solid = true
  Symmetric = false
FEATURE [Part::Extrusion] Extrusion088
  Base = -> Face056
  Dir = (2.8e-15,-19.9,2.2e-15)
  DirMode = 0
  FaceMakerClass = Part::FaceMakerBullseye
  LengthFwd = 0
  LengthRev = 0
  Solid = true
  Symmetric = false
FEATURE [Part::Refine] Extrusion084
  Source = -> Extrusion088
FEATURE [Part::MultiFuse] Fusion005002002014004003003002009002010004002003006003008008004007002004008002005021002008
  Shapes = -> [Extrusion050,Extrusion084]
FEATURE [Part::MultiFuse] Fusion005002002014004003003002009002010004002003006003008008004007002004008002005021002026
  Placement = pos=(-5.197e-12,-20.9,2.73057e-07) rot=(0,0,1;0rad)
  Shapes = -> [Fusion005002002014004003003002009002010004002003006003008008004007002004008002005021002011,Extrusion073]
FEATURE [Part::Extrusion] Extrusion089
  Base = -> Circle006
  Dir = (0,1.86269e-10,-7)
  DirMode = 0
  FaceMakerClass = Part::FaceMakerBullseye
  LengthFwd = 0
  LengthRev = 0
  Solid = true
  Symmetric = false
FEATURE [Part::Extrusion] Extrusion090
  Base = -> Circle007
  Dir = (-2.85319e-10,-4.50839e-08,-7)
  DirMode = 0
  FaceMakerClass = Part::FaceMakerBullseye
  LengthFwd = 0
  LengthRev = 0
  Solid = true
  Symmetric = false
FEATURE [Part::Feature] Face061
  shape: bbox 2.001 x 19.9 x 0.0008489 mm, 1 faces, 0 solids (baked)
FEATURE [Part::Extrusion] Extrusion056
  Base = -> Face061
  Dir = (9.73293e-10,1.1e-15,9.7)
  DirMode = 0
  FaceMakerClass = Part::FaceMakerBullseye
  LengthFwd = 0
  LengthRev = 0
  Solid = true
  Symmetric = false
FEATURE [Part::MultiFuse] Fusion005002002014004003003002009002010004002003006003008008004007002004008002005021002022
  Shapes = -> [Extrusion056,Extrusion077]
FEATURE [Part::MultiFuse] Fusion005002002014004003003002009002010004002003006003008008004007002004008002005021002006
  Shapes = -> [Fusion005002002014004003003002009002010004002003006003008008004007002004008002005021002008,Fusion005002002014004003003002009002010004002003006003008008004007002004008002005021002022]
FEATURE [Part::Part2DObjectPython] Wire003  # Draft 2D object (typed FeaturePython)
  Area = 63.4773
  ChamferSize = 0
  Closed = true
  End = (11.3133,28,-1.5)
  FilletRadius = 0
  Length = 49.1096
  MakeFace = true
  Placement = pos=(8.31326,28,-1.5) rot=(0.57735,0.57735,0.57735;2.0944rad)
  Points = (4) [(0,0,0),(-1.7945e-07,20,-1.24955e-09),(-1.7945e-07,22.3182,3),(-1.7945e-07,-2.4067e-07,3)]
  Start = (8.31326,28,-1.5)
  Subdivisions = 0
FEATURE [Part::Extrusion] Extrusion049
  Base = -> Wire003
  Dir = (3.07294e-07,11,-2.91789e-08)
  DirMode = 0
  FaceMakerClass = Part::FaceMakerBullseye
  LengthFwd = 0
  LengthRev = 0
  Solid = true
  Symmetric = false
FEATURE [Part::Cut] Cut023008
  Base = -> Cut023010
  Tool = -> Extrusion049
FEATURE [Part::MultiFuse] Fusion005002002014004003003002009002010004002003006003008008004007002004008002005021002028
  Shapes = -> [Cut023017,Extrusion069]
FEATURE [Part::MultiFuse] Fusion005002002014004003003002009002010004002003006003008008004007002004008002005021002004
  Shapes = -> [Extrusion065,Extrusion059,Fusion005002002014004003003002009002010004002003006003008008004007002004008002005021002028]
FEATURE [Part::Cut] Cut023019
  Base = -> Fusion005002002014004003003002009002010004002003006003008008004007002004008002005021002004
  Tool = -> Cone001
FEATURE [Part::Refine] Cut023014
  Source = -> Cut023019
FEATURE [Part::Cut] Cut023012
  Base = -> Cut023014
  Tool = -> Extrusion081
FEATURE [Part::MultiFuse] Fusion005002002014004003003002009002010004002003006003008008004007002004008002005021002021
  Shapes = -> [Extrusion071,Cut023012]
FEATURE [Part::Cut] Cut023002
  Base = -> Fusion005002002014004003003002009002010004002003006003008008004007002004008002005021002021
  Tool = -> Extrusion062
FEATURE [Part::Cut] Cut023011
  Base = -> Cut023002
  Tool = -> Extrusion078
FEATURE [Part::Cut] Cut023013
  Base = -> Cut023011
  Tool = -> Extrusion061
FEATURE [Part::Refine] Cut023006
  Source = -> Cut023013
FEATURE [Part::MultiFuse] Fusion005002002014004003003002009002010004002003006003008008004007002004008002005021002023
  Shapes = -> [Cut023006,Extrusion082]
FEATURE [Part::MultiFuse] Fusion005002002014004003003002009002010004002003006003008008004007002004008002005021002005
  Shapes = -> [Cut023003,Fusion005002002014004003003002009002010004002003006003008008004007002004008002005021002023]
FEATURE [Part::MultiFuse] Fusion005002002014004003003002009002010004002003006003008008004007002004008002005021002010
  Shapes = -> [Fusion005002002014004003003002009002010004002003006003008008004007002004008002005021002005,Extrusion058]
FEATURE [Part::MultiFuse] Fusion005002002014004003003002009002010004002003006003008008004007002004008002005021002017
  Shapes = -> [Fusion005002002014004003003002009002010004002003006003008008004007002004008002005021002006,Fusion005002002014004003003002009002010004002003006003008008004007002004008002005021002010]
FEATURE [Part::MultiFuse] Fusion005002002014004003003002009002010004002003006003008008004007002004008002005021002027
  Shapes = -> [Fusion005002002014004003003002009002010004002003006003008008004007002004008002005021002017,Extrusion054,Fusion005002002014004003003002009002010004002003006003008008004007002004008002005021002026,Extrusion060]
FEATURE [Part::Extrusion] Extrusion091
  Base = -> Face038
  Dir = (-6.81326,1.5e-15,2.77705e-10)
  DirMode = 0
  FaceMakerClass = Part::FaceMakerBullseye
  LengthFwd = 0
  LengthRev = 0
  Solid = true
  Symmetric = false
FEATURE [Part::MultiFuse] Fusion005002002014004003003002009002010004002003006003008008004007002004008002005021002009
  Shapes = -> [Cut023008,Extrusion091]
FEATURE [Part::MultiFuse] Fusion005002002014004003003002009002010004002003006003008008004007002004008002005021002018
  Shapes = -> [Fusion005002002014004003003002009002010004002003006003008008004007002004008002005021002027,Fusion005002002014004003003002009002010004002003006003008008004007002004008002005021002012,Fusion005002002014004003003002009002010004002003006003008008004007002004008002005021002009,Extrusion053]
FEATURE [Part::MultiFuse] Fusion005002002014004003003002009002010004002003006003008008004007002004008002005021002015
  Shapes = -> [Fusion005002002014004003003002009002010004002003006003008008004007002004008002005021002018,Extrusion067]
FEATURE [Part::MultiFuse] Fusion005002002014004003003002009002010004002003006003008008004007002004008002005021002014
  Shapes = -> [Fusion005002002014004003003002009002010004002003006003008008004007002004008002005021002015,Fusion005002002014004003003002009002010004002003006003008008004007002004008002005021002007]
FEATURE [Part::Refine] Fusion005002002014004003003002009002010004002003006003008008004007002004008002005021002016
  Source = -> Fusion005002002014004003003002009002010004002003006003008008004007002004008002005021002014
FEATURE [Part::MultiFuse] Fusion005002002014004003003002009002010004002003006003008008004007002004008002005021002013
  Shapes = -> [Fusion005002002014004003003002009002010004002003006003008008004007002004008002005021002016,Extrusion064]
FEATURE [Part::Cut] Cut023009
  Base = -> Fusion005002002014004003003002009002010004002003006003008008004007002004008002005021002013
  Tool = -> Extrusion070
FEATURE [Part::MultiFuse] Fusion005002002014004003003002009002010004002003006003008008004007002004008002005021002025
  Shapes = -> [Extrusion066,Cut023009]
FEATURE [Part::Cut] Cut023016
  Base = -> Fusion005002002014004003003002009002010004002003006003008008004007002004008002005021002025
  Tool = -> Extrusion089
FEATURE [Part::Cut] Cut023015
  Base = -> Cut023016
  Tool = -> Extrusion090
FEATURE [Part::Refine] Cut023018
  Source = -> Cut023015
FEATURE [Part::Feature] Face062
  shape: bbox 181.8 x 0.0008491 x 35.7 mm, 1 faces, 0 solids (baked)
FEATURE [Part::Extrusion] Extrusion048
  Base = -> Face062
  Dir = (-3.22717e-10,-1.5,3.15143e-09)
  DirMode = 0
  FaceMakerClass = Part::FaceMakerBullseye
  LengthFwd = 0
  LengthRev = 0
  Solid = true
  Symmetric = false
FEATURE [Part::Cut] Cut023007
  Base = -> Cut023018
  Placement = pos=(223.491,-3.51436e-08,3.11426e-07) rot=(0,0,1;0rad)
  Tool = -> Extrusion048
FEATURE [Part::Part2DObjectPython] Rectangle020  # Draft 2D object (typed FeaturePython)
  Area = 1254.41
  ChamferSize = 0
  Columns = 1
  FilletRadius = 0
  Height = 16.0376
  Length = 78.217
  MakeFace = true
  Placement = pos=(228.13,72.1,29.5908) rot=(-1,0,0;1.5708rad)
  Rows = 1
FEATURE [Part::FeaturePython] Slice002  # WARN: FeaturePython — macro-defined, semantics opaque (R4)
  Base = -> Cut023007
  Mode = 1
  Tolerance = 0
  Tools = -> [Rectangle020]
FEATURE [Part::FeaturePython] Slice002_child0  label="Slice002.0"  # WARN: FeaturePython — macro-defined, semantics opaque (R4)
  Base = -> Slice002
  FilterType = 1
  Invert = false
  OverrideMaxVal = 0
  WindowFrom = 80
  WindowTo = 100
  items = 0
FEATURE [Part::Feature] Face063
  shape: bbox 1.381 x 0.0005988 x 1.397 mm, 1 faces, 0 solids (baked)
FEATURE [Part::Extrusion] Extrusion092
  Base = -> Face063
  Dir = (-2.24497e-10,-1.5,4.2687e-09)
  DirMode = 0
  FaceMakerClass = Part::FaceMakerBullseye
  LengthFwd = 0
  LengthRev = 0
  Solid = true
  Symmetric = false
FEATURE [Part::Cut] Cut023020
  Base = -> Slice002_child0
  Tool = -> Extrusion092
FEATURE [Part::Feature] Face064
  shape: bbox 1.576 x 0.0005988 x 2.148 mm, 1 faces, 0 solids (baked)
FEATURE [Part::Extrusion] Extrusion093
  Base = -> Face064
  Dir = (-2.24497e-10,-1.5,4.2687e-09)
  DirMode = 0
  FaceMakerClass = Part::FaceMakerBullseye
  LengthFwd = 0
  LengthRev = 0
  Solid = true
  Symmetric = false
FEATURE [Part::Cut] Cut023021
  Base = -> Cut023020
  Tool = -> Extrusion093
FEATURE [Part::Feature] Face065
  shape: bbox 1.727 x 0.0005988 x 1.611 mm, 1 faces, 0 solids (baked)
FEATURE [Part::Extrusion] Extrusion094
  Base = -> Face065
  Dir = (6.35716e-09,-1.5,-2.86574e-09)
  DirMode = 0
  FaceMakerClass = Part::FaceMakerBullseye
  LengthFwd = 0
  LengthRev = 0
  Solid = true
  Symmetric = false
FEATURE [Part::Cut] Cut023022
  Base = -> Cut023021
  Tool = -> Extrusion094
FEATURE [Part::Feature] Face066
  shape: bbox 2.064 x 9.476e-05 x 0.9418 mm, 1 faces, 0 solids (baked)
FEATURE [Part::Extrusion] Extrusion095
  Base = -> Face066
  Dir = (0,-1.5,-2.85948e-09)
  DirMode = 0
  FaceMakerClass = Part::FaceMakerBullseye
  LengthFwd = 0
  LengthRev = 0
  Solid = true
  Symmetric = false
FEATURE [Part::Cut] Cut023023
  Base = -> Cut023022
  Tool = -> Extrusion095
FEATURE [Part::Feature] Face067
  shape: bbox 2.064 x 9.476e-05 x 0.9418 mm, 1 faces, 0 solids (baked)
FEATURE [Part::Extrusion] Extrusion096
  Base = -> Face067
  Dir = (0,-1.5,-2.85948e-09)
  DirMode = 0
  FaceMakerClass = Part::FaceMakerBullseye
  LengthFwd = 0
  LengthRev = 0
  Solid = true
  Symmetric = false
FEATURE [Part::Cut] Cut023024
  Base = -> Cut023023
  Tool = -> Extrusion096
FEATURE [Part::Feature] Face068
  Placement = pos=(343.145,70.35,1.9) rot=(1,0,0;1.5708rad)
  shape: bbox 12.11 x 0.0005983 x 5.601 mm, 1 faces, 0 solids (baked)
FEATURE [Part::Extrusion] Extrusion097
  Base = -> Face068
  Dir = (2.417e-12,-0.29991,5.53837e-10)
  DirMode = 0
  FaceMakerClass = Part::FaceMakerBullseye
  LengthFwd = 0
  LengthRev = 0
  Solid = true
  Symmetric = false
FEATURE [Part::MultiFuse] Fusion005002002014004003003002009002010004002003006003008008004007002004008002005021002029
  Shapes = -> [Cut023024,Extrusion097]
FEATURE [App::DocumentObjectGroup] GrExplode_Slice002  label="Exploded Slice002"
  Group = -> [Fusion005002002014004003003002009002010004002003006003008008004007002004008002005021002029]
